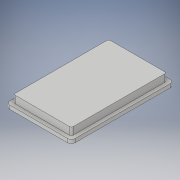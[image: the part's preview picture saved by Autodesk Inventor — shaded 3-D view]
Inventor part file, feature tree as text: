
AUTODESK INVENTOR PART (.ipt)
format: ipt  version: 2019 (Build 230136000, 136)  size: 266,240 bytes
history: native  units: in
note: dims shown in document units (in); Inventor stores cm internally (conversion verified against a paired STEP export)
features: sketch x3, extrude x2, fillet x2
ambient origin geometry x8: Origin, YZ Plane, XZ Plane, XY Plane, X Axis, Y Axis, Z Axis, Center Point
bodies: Solid1 (feature_tree)
feature tree (7):
  sketch  "Sketch1"  dims[d0=0.689in d1=1.0827in]
  extrude  "Extrusion1"  Depth=1.0827in
  extrude  "Extrusion2"  Depth=0.0394in
  fillet  "Fillet1"  Radius=0.0394in
  fillet  "Fillet2"  Radius=0.6102in
  sketch  "Sketch2"  dims[d2=0.0394in d3=0.0in d4=0.0394in d5=0.0394in d6=0.6102in]
  sketch  "Sketch3"  dims[d7=1.0039in d8=0.0787in d9=0.0in d10=0.0394in d11=0.0197in]
